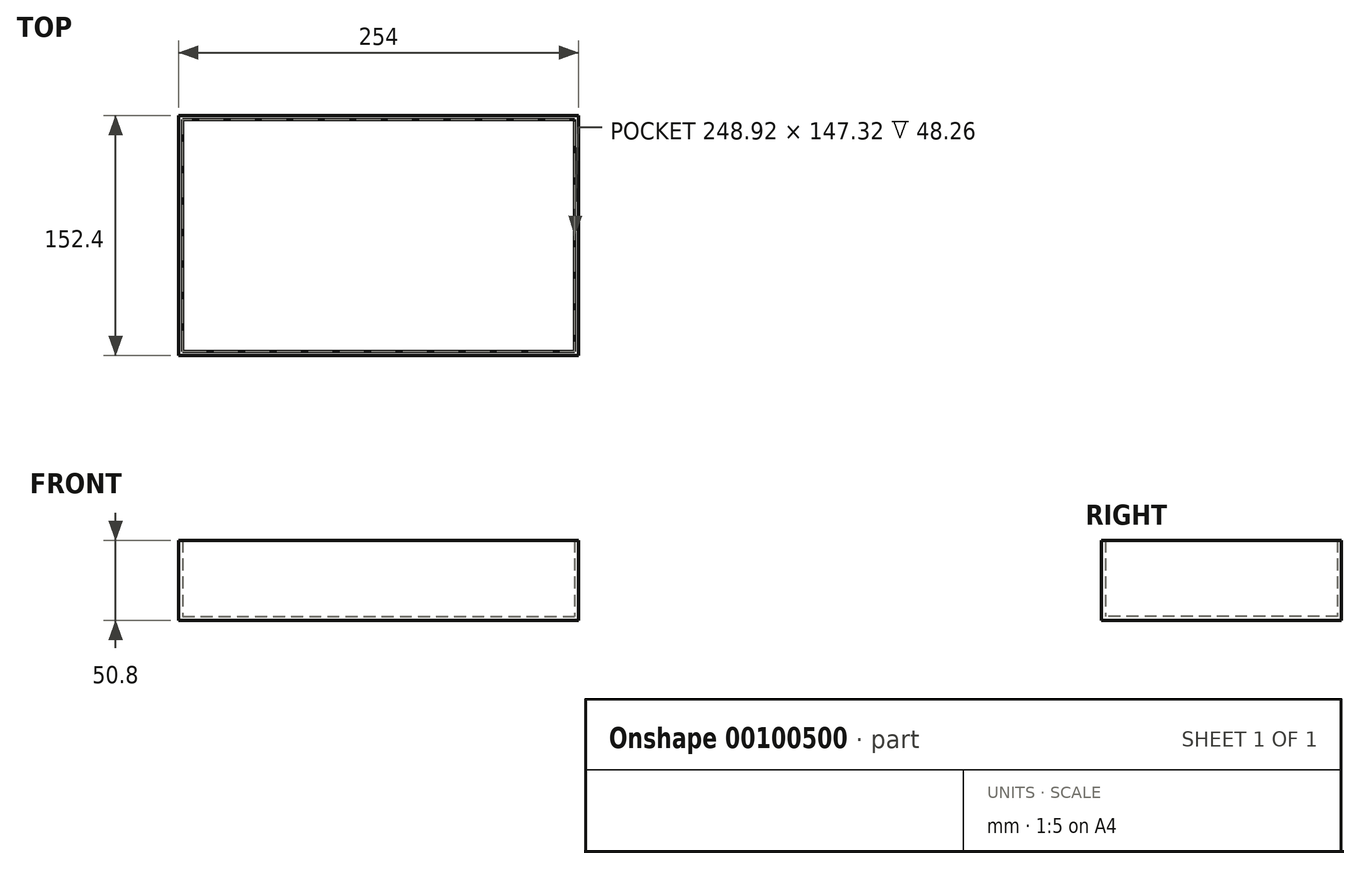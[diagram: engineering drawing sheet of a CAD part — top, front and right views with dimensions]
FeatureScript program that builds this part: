
annotation { "Feature Type Name" : "Feature", "Feature Type Description" : "" }
export const myFeature = defineFeature(function(context is Context, id is Id, definition is map)
    precondition{}
    {
        {
            var Q0;
            Q0=qCreatedBy(makeId("Top.planeOp"),FACE);
            var sketch = newSketch(context, id + "F0", { "sketchPlane" : qUnion([Q0])});
            skLineSegment(sketch, "E0.bottom", {"start": v(-127, 76.2) * mm, "end": v(127, 76.2) * mm});
            skLineSegment(sketch, "E0.top", {"start": v(-127, -76.2) * mm, "end": v(127, -76.2) * mm});
            skLineSegment(sketch, "E0.left", {"start": v(-127, 76.2) * mm, "end": v(-127, -76.2) * mm});
            skLineSegment(sketch, "E0.right", {"start": v(127, 76.2) * mm, "end": v(127, -76.2) * mm});
            skPoint(sketch, "E0.middle", {"position": v(0, 0) * mm});
            skSolve(sketch);
        }
        {
            var Q0;
            Q0=makeQuery(id+"F0.imprint","IMPRINT",FACE,{"disambiguationData":[TD([[makeQuery(id+"F0.imprint","IMPRINT",EDGE,{"derivedFrom":sQuery(id+"F0.wireOp",EDGE,"E0.bottom")}),-1.0]])]});
            extrude(context, id + "F1", {"entities" : qUnion([Q0]), "depth" : 50.8 * mm, "offsetDistance" : 25.4 * mm});
        }
        {
            var Q0;
            Q0=makeQuery(id+"F1.opExtrude","CAP_FACE",FACE,{"disambiguationData":[OSD([sQuery(id+"F0.wireOp",EDGE,"E0.bottom"),sQuery(id+"F0.wireOp",EDGE,"E0.top"),sQuery(id+"F0.wireOp",EDGE,"E0.left"),sQuery(id+"F0.wireOp",EDGE,"E0.right")])],"isStart":false});
            shell(context, id + "F2", {"entities" : qUnion([Q0]), "thickness" : 2.54 * mm});
        }
    });
